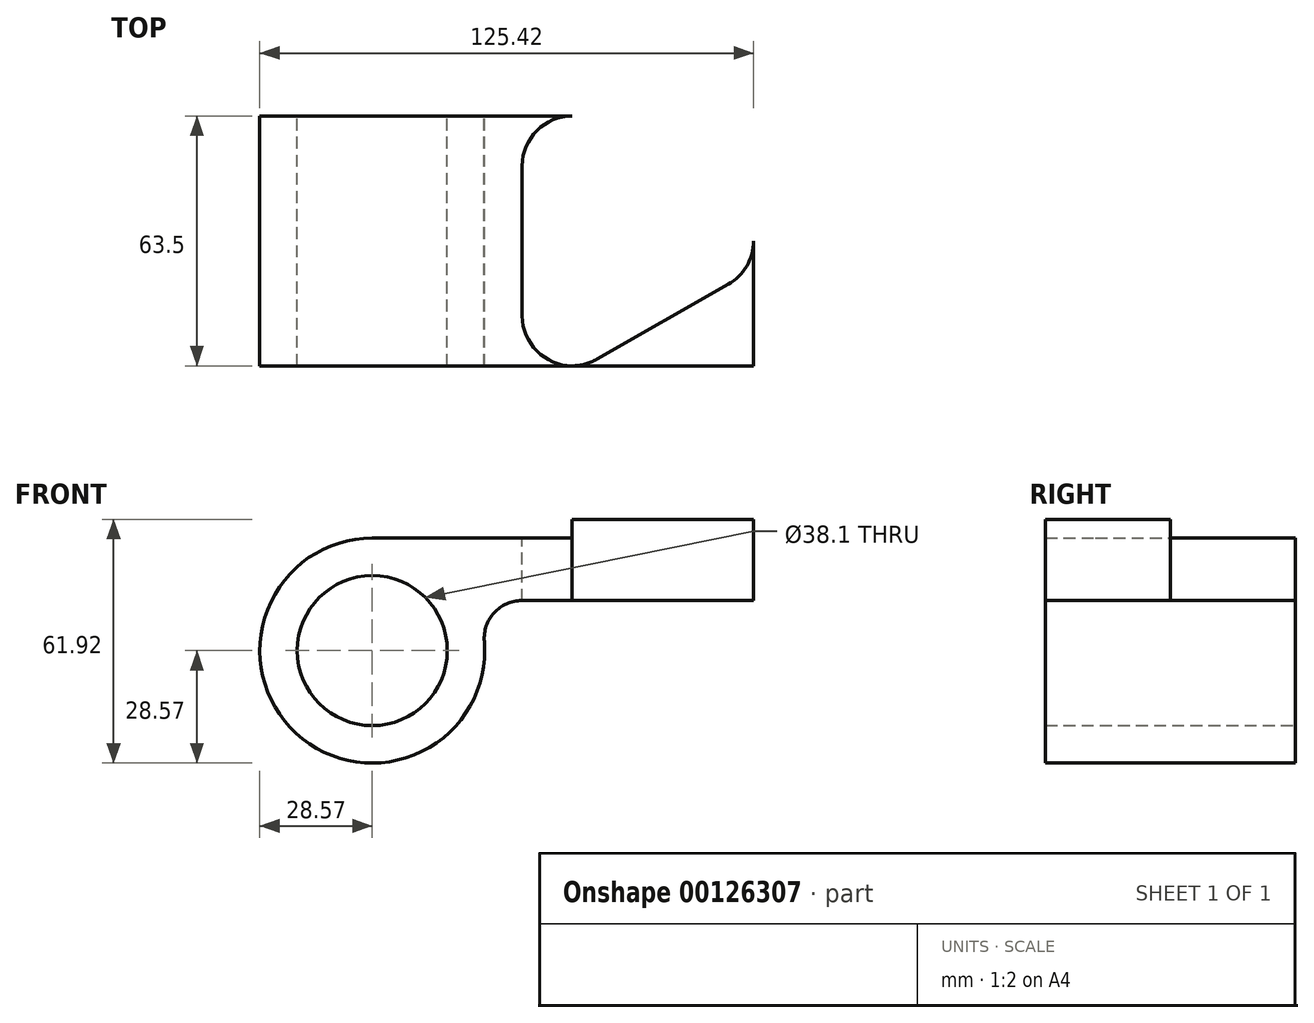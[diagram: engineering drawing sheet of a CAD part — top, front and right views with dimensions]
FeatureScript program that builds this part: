
annotation { "Feature Type Name" : "Feature", "Feature Type Description" : "" }
export const myFeature = defineFeature(function(context is Context, id is Id, definition is map)
    precondition{}
    {
        {
            var Q0;
            Q0=qCreatedBy(makeId("Front.planeOp"),FACE);
            var sketch = newSketch(context, id + "F0", { "sketchPlane" : qUnion([Q0])});
            skLineSegment(sketch, "E0", {"start": v(28.58, 0) * mm, "end": v(28.58, 0) * mm});
            skCircle(sketch, "E1", {"center": v(0, 0) * mm, "radius": 19.05 * mm});
            skLineSegment(sketch, "E2", {"start": v(0, 28.58) * mm, "end": v(50.8, 28.58) * mm});
            skLineSegment(sketch, "E3", {"start": v(50.8, 28.58) * mm, "end": v(50.8, 13.85) * mm, "construction": true});
            skLineSegment(sketch, "E4", {"start": v(0, 0) * mm, "end": v(0, -40.23) * mm, "construction": true});
            skArc(sketch, "E5", {"start": v(0, 28.58) * mm, "mid": v(-19.35, -21.03) * mm, "end": v(28.48, 2.38) * mm});
            skArc(sketch, "E6", {"start": v(28.48, 2.38) * mm, "mid": v(30.96, 9.62) * mm, "end": v(37.97, 12.7) * mm});
            skLineSegment(sketch, "E7", {"start": v(37.97, 12.7) * mm, "end": v(96.85, 12.7) * mm});
            skLineSegment(sketch, "E8", {"start": v(16, -23.68) * mm, "end": v(69.85, 12.7) * mm});
            skLineSegment(sketch, "E9", {"start": v(84.15, 12.7) * mm, "end": v(84.15, 28.58) * mm, "construction": true});
            skLineSegment(sketch, "E10", {"start": v(50.8, 28.58) * mm, "end": v(84.15, 28.58) * mm});
            skLineSegment(sketch, "E11", {"start": v(96.85, 12.7) * mm, "end": v(96.85, 28.58) * mm});
            skLineSegment(sketch, "E12", {"start": v(96.85, 28.58) * mm, "end": v(84.15, 28.58) * mm});
            skLineSegment(sketch, "E13", {"start": v(96.85, 28.58) * mm, "end": v(96.85, 33.35) * mm});
            skLineSegment(sketch, "E14", {"start": v(96.85, 33.35) * mm, "end": v(38.1, 33.35) * mm});
            skLineSegment(sketch, "E15", {"start": v(38.1, 28.58) * mm, "end": v(38.1, 33.35) * mm});
            skSolve(sketch);
        }
        {
            var Q0;
            Q0=makeQuery(id+"F0.imprint","IMPRINT",FACE,{"disambiguationData":[TD([[makeQuery(id+"F0.imprint","IMPRINT",EDGE,{"derivedFrom":sQuery(id+"F0.wireOp",EDGE,"E1")}),-1.0]])]});
            extrude(context, id + "F1", {"entities" : qUnion([Q0]), "endBound" : BoundingType.SYMMETRIC, "depth" : 63.5 * mm});
        }
        {
            var Q0;
            {var subQ0=sQuery(id+"F0.wireOp",EDGE,"E6");Q0=makeQuery(id+"F0.imprint","IMPRINT",FACE,{"disambiguationData":[TD([[makeQuery(id+"F0.imprint","IMPRINT",EDGE,{"derivedFrom":subQ0}),-1.0]])]});}
            extrude(context, id + "F2", {"entities" : qUnion([Q0]), "operationType" : NewBodyOperationType.ADD, "endBound" : BoundingType.SYMMETRIC, "depth" : 9.52 * mm});
        }
        {
            var Q0;
            {var subQ0=sQuery(id+"F0.wireOp",EDGE,"E10");Q0=makeQuery(id+"F0.imprint","IMPRINT",FACE,{"disambiguationData":[TD([[makeQuery(id+"F0.imprint","IMPRINT",EDGE,{"derivedFrom":subQ0}),1.0]])]});}
            extrude(context, id + "F3", {"entities" : qUnion([Q0]), "operationType" : NewBodyOperationType.ADD, "endBound" : BoundingType.SYMMETRIC, "depth" : 63.5 * mm});
        }
        {
            var Q0;
            Q0=makeQuery(id+"F3.opExtrude","SWEPT_FACE",FACE,{"disambiguationData":[OSD([sQuery(id+"F0.wireOp",EDGE,"E14")])]});
            var sketch = newSketch(context, id + "F4", { "sketchPlane" : qUnion([Q0])});
            skLineSegment(sketch, "E16.0.3", {"start": v(0, 31.75) * mm, "end": v(0, -31.75) * mm});
            skPoint(sketch, "E16.0.2.start.orphan", {"position": v(38.1, 31.75) * mm});
            skPoint(sketch, "E16.0.0.end.orphan", {"position": v(38.1, -31.75) * mm});
            skLineSegment(sketch, "E17", {"start": v(50.8, 0) * mm, "end": v(50.8, 31.75) * mm, "construction": true});
            skLineSegment(sketch, "E18", {"start": v(50.8, 0) * mm, "end": v(50.8, -31.75) * mm, "construction": true});
            skCircle(sketch, "E19", {"center": v(50.8, -19.05) * mm, "radius": 5.56 * mm});
            skCircle(sketch, "E20", {"center": v(50.8, 19.05) * mm, "radius": 5.56 * mm});
            skLineSegment(sketch, "E21", {"start": v(41.99, 0) * mm, "end": v(116.12, 0) * mm, "construction": true});
            skCircle(sketch, "E22", {"center": v(84.15, 0) * mm, "radius": 5.56 * mm});
            skLineSegment(sketch, "E23.0", {"start": v(38.1, -31.75) * mm, "end": v(38.1, 31.75) * mm});
            skArc(sketch, "E24", {"start": v(38.1, 19.05) * mm, "mid": v(44.42, 30.03) * mm, "end": v(57.1, 30.08) * mm});
            skArc(sketch, "E25", {"start": v(38.1, -19.05) * mm, "mid": v(44.42, -30.03) * mm, "end": v(57.1, -30.08) * mm});
            skPoint(sketch, "E25.startSnap0", {"position": v(38.1, 0) * mm});
            skArc(sketch, "E26", {"start": v(96.85, 0) * mm, "mid": v(95.13, -6.38) * mm, "end": v(90.45, -11.03) * mm});
            skLineSegment(sketch, "E27", {"start": v(57.1, -30.08) * mm, "end": v(90.45, -11.03) * mm});
            skArc(sketch, "E28", {"start": v(96.85, 0) * mm, "mid": v(95.13, 6.38) * mm, "end": v(90.45, 11.03) * mm});
            skLineSegment(sketch, "E29", {"start": v(57.1, 30.08) * mm, "end": v(91.04, 10.7) * mm});
            skPoint(sketch, "E29.endSnap0", {"position": v(91.04, 10.67) * mm});
            skSolve(sketch);
        }
        {
            var Q0;
            {var subQ0=sQuery(id+"F4.wireOp",EDGE,"E23.0");var subQ1=makeQuery(id+"F3.opExtrude","CAP_EDGE",EDGE,{"disambiguationData":[OSD([sQuery(id+"F0.wireOp",EDGE,"E14")])],"isStart":false});var subQ2=makeQuery(id+"F4.imprint","INTERSECT",VERTEX,{"derivedFrom":[subQ1,subQ0]});Q0=makeQuery(id+"F4.imprint","IMPRINT",FACE,{"disambiguationData":[TD([[makeQuery(id+"F4.imprint","IMPRINT",EDGE,{"disambiguationData":[TD([[subQ2,-1.0]])],"derivedFrom":subQ0}),-1.0]])]});}
            var Q1;
            {var subQ0=sQuery(id+"F4.wireOp",EDGE,"E23.0");var subQ1=makeQuery(id+"F3.opExtrude","CAP_EDGE",EDGE,{"disambiguationData":[OSD([sQuery(id+"F0.wireOp",EDGE,"E14")])],"isStart":true});var subQ2=makeQuery(id+"F4.imprint","INTERSECT",VERTEX,{"derivedFrom":[subQ1,subQ0]});Q1=makeQuery(id+"F4.imprint","IMPRINT",FACE,{"disambiguationData":[TD([[makeQuery(id+"F4.imprint","IMPRINT",EDGE,{"disambiguationData":[TD([[subQ2,1.0]])],"derivedFrom":subQ0}),-1.0]])]});}
            var Q2;
            Q2=makeQuery(id+"F1.opExtrude","SWEPT_FACE",FACE,{"disambiguationData":[OSD([sQuery(id+"F0.wireOp",EDGE,"E2"),sQuery(id+"F0.wireOp",EDGE,"E10"),sQuery(id+"F0.wireOp",EDGE,"E12")])]});
            extrude(context, id + "F5", {"entities" : qUnion([Q0, Q1]), "operationType" : NewBodyOperationType.REMOVE, "endBound" : BoundingType.UP_TO_SURFACE, "oppositeDirection" : true, "endBoundEntityFace" : qUnion([Q2]), "depth" : 4.78 * mm});
        }
        {
            var Q0;
            {var subQ3=sQuery(id+"F4.wireOp",EDGE,"E28");Q0=makeQuery(id+"F4.imprint","IMPRINT",FACE,{"disambiguationData":[TD([[makeQuery(id+"F4.imprint","IMPRINT",EDGE,{"derivedFrom":subQ3}),-1.0]])]});}
            var Q1;
            {var subQ0=sQuery(id+"F4.wireOp",EDGE,"E26");Q1=makeQuery(id+"F4.imprint","IMPRINT",FACE,{"disambiguationData":[TD([[makeQuery(id+"F4.imprint","IMPRINT",EDGE,{"derivedFrom":subQ0}),1.0]])]});}
            var Q2;
            Q2=makeQuery(id+"F4.imprint","IMPRINT",FACE,{"disambiguationData":[TD([[makeQuery(id+"F4.imprint","IMPRINT",EDGE,{"derivedFrom":sQuery(id+"F4.wireOp",EDGE,"E20")}),1.0]])]});
            var Q3;
            Q3=makeQuery(id+"F4.imprint","IMPRINT",FACE,{"disambiguationData":[TD([[makeQuery(id+"F4.imprint","IMPRINT",EDGE,{"derivedFrom":sQuery(id+"F4.wireOp",EDGE,"E19")}),1.0]])]});
            var Q4;
            Q4=makeQuery(id+"F4.imprint","IMPRINT",FACE,{"disambiguationData":[TD([[makeQuery(id+"F4.imprint","IMPRINT",EDGE,{"derivedFrom":sQuery(id+"F4.wireOp",EDGE,"E22")}),1.0]])]});
            extrude(context, id + "F6", {"entities" : qUnion([Q0, Q1, Q2, Q3, Q4]), "operationType" : NewBodyOperationType.REMOVE, "endBound" : BoundingType.THROUGH_ALL, "oppositeDirection" : true, "depth" : 25.4 * mm});
        }
    });
